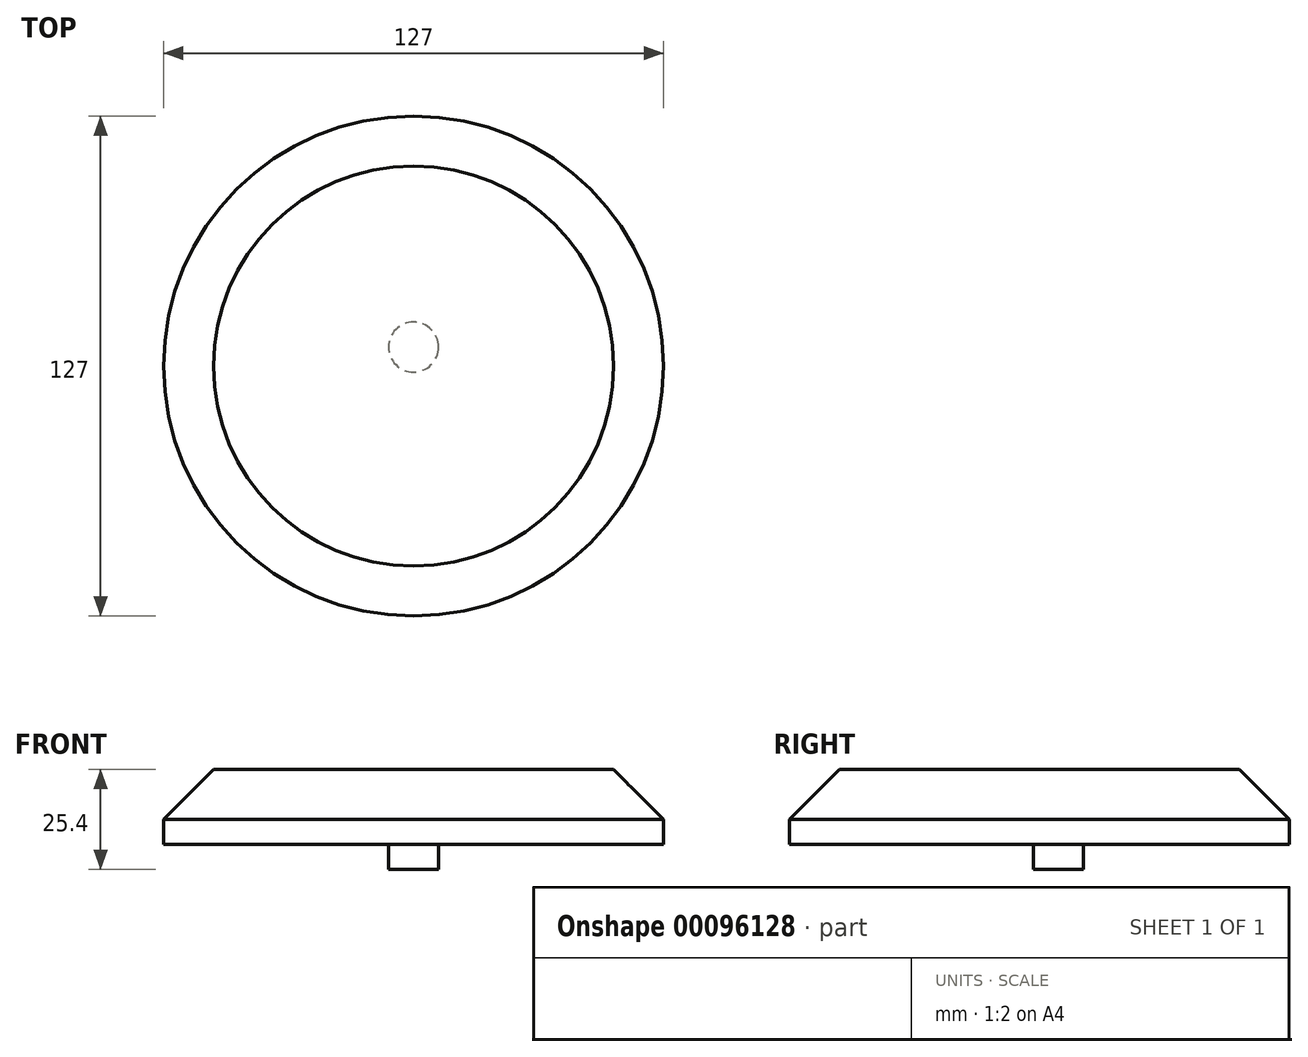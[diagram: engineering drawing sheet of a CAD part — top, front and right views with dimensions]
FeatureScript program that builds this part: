
annotation { "Feature Type Name" : "Feature", "Feature Type Description" : "" }
export const myFeature = defineFeature(function(context is Context, id is Id, definition is map)
    precondition{}
    {
        {
            var Q0;
            Q0=qCreatedBy(makeId("Top.planeOp"),FACE);
            var sketch = newSketch(context, id + "F0", { "sketchPlane" : qUnion([Q0])});
            skCircle(sketch, "E0", {"center": v(0, -4.81) * mm, "radius": 63.5 * mm});
            skSolve(sketch);
        }
        {
            var Q0;
            Q0=qSketchRegion(id+"F0",true);
            extrude(context, id + "F1", {"entities" : qUnion([Q0]), "depth" : 19.05 * mm});
        }
        {
            var Q0;
            Q0=makeQuery(id+"F1.opExtrude","CAP_FACE",FACE,{"disambiguationData":[OSD([sQuery(id+"F0.wireOp",EDGE,"E0")])],"isStart":true});
            var sketch = newSketch(context, id + "F2", { "sketchPlane" : qUnion([Q0])});
            skCircle(sketch, "E1", {"center": v(0, 0) * mm, "radius": 6.35 * mm});
            skSolve(sketch);
        }
        {
            var Q0;
            Q0=qSketchRegion(id+"F2",true);
            extrude(context, id + "F3", {"entities" : qUnion([Q0]), "operationType" : NewBodyOperationType.ADD, "depth" : 6.35 * mm});
        }
        {
            var Q0;
            Q0=makeQuery(id+"F1.opExtrude","CAP_EDGE",EDGE,{"disambiguationData":[OSD([sQuery(id+"F0.wireOp",EDGE,"E0")])],"isStart":false});
            chamfer(context, id + "F4", {"entities" : qUnion([Q0]), "width" : 12.7 * mm, "tangentPropagation" : true});
        }
    });
